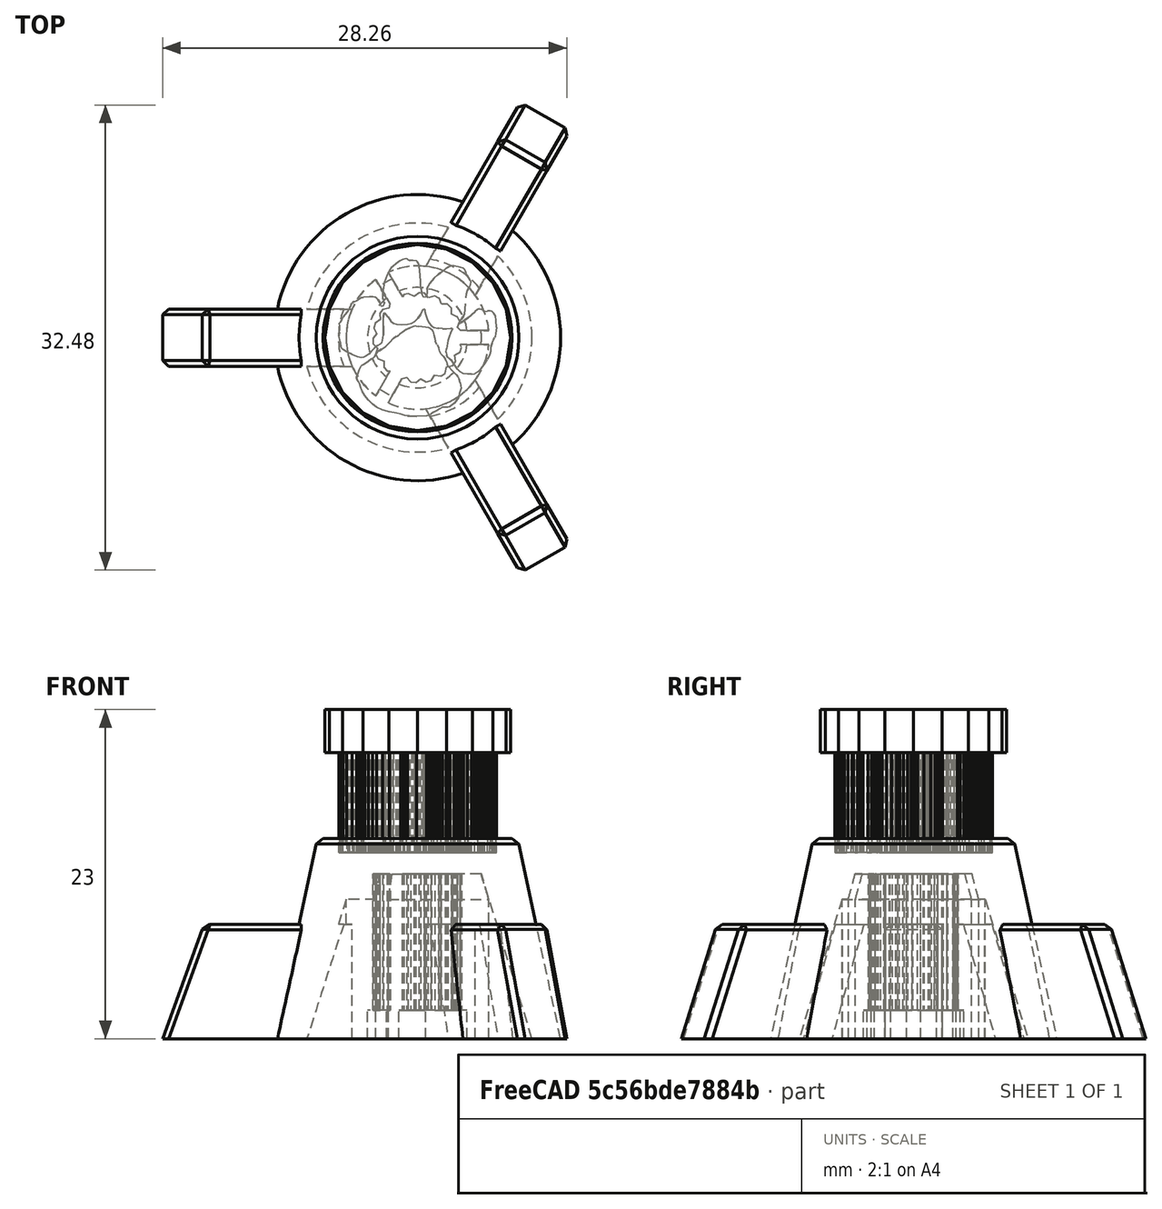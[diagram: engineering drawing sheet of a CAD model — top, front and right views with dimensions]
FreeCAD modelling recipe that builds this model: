
FCSTD DOCUMENT  (FreeCAD 0.18R16146 (Git))
Label: lcd-knob
License: All rights reserved
LicenseURL: http://en.wikipedia.org/wiki/All_rights_reserved
objects: Part::Feature×7, Part::Cut×4, Part::Cylinder×3, Part::MultiCommon×3, Part::Cone×2, Part::Box×2, Part::MultiFuse×2, Part::Chamfer×1
note: 24 computed .brp shape members not serialized (recipe doc carries the construction recipe); baked Part::Feature solids carry a one-line shape summary decoded from their .brp

FEATURE [Part::Feature] Powerful_Habbi001001_solid  label="hole"
  Placement = pos=(0.2,10.2,0) rot=(0,0,1;0rad)
  shape: bbox 7.502 x 7.501 x 12.43 mm, 81 faces (baked)
FEATURE [Part::Cylinder] Cylinder
  Angle = 360
  AttacherType = Attacher::AttachEngine3D
  Height = 17
  Radius = 3.5
FEATURE [Part::MultiCommon] Common  label="knob-hole"
  Shapes = -> [Cylinder,Powerful_Habbi001001_solid]
FEATURE [Part::Cone] Cone
  Angle = 360
  AttacherType = Attacher::AttachEngine3D
  Height = 14
  Radius1 = 10
  Radius2 = 7
FEATURE [Part::Cylinder] Cylinder001
  Angle = 360
  AttacherType = Attacher::AttachEngine3D
  Height = 13
  Radius = 5
FEATURE [Part::Cut] Cut
  Base = -> Cylinder001
  Tool = -> Common
FEATURE [Part::Cone] Cone001
  Angle = 360
  AttacherType = Attacher::AttachEngine3D
  Height = 13
  Radius1 = 8
  Radius2 = 4
FEATURE [Part::Cut] Cut001
  Base = -> Cone
  Tool = -> Cone001
FEATURE [Part::Box] Box  label="Cube"
  AttacherType = Attacher::AttachEngine3D
  Height = 12.43
  Length = 6
  Placement = pos=(0,-0.5,0) rot=(0,0,1;0rad)
  Width = 1
FEATURE [Part::Cut] Cut002
  Base = -> Cut
  Tool = -> Box
FEATURE [Part::Box] Box001  label="Cube001"
  AttacherType = Attacher::AttachEngine3D
  Height = 8
  Length = 14
  Placement = pos=(-18,-2,0) rot=(0,0,1;0rad)
  Width = 4
FEATURE [Part::Feature] Box002001  label="Cube003"
  Placement = pos=(0,0,2) rot=(0,0,1;0rad)
  shape: bbox 21.02 x 4 x 26.4 mm, 6 faces (baked)
FEATURE [Part::Cut] Cut003
  Base = -> Box001
  Tool = -> Box002001
FEATURE [Part::Feature] Cut003001  label="Cut004"
  Placement = pos=(0,0,0) rot=(0,0,1;4.18879rad)
  shape: bbox 10.38 x 13.98 x 8 mm, 6 faces (baked)
FEATURE [Part::Feature] Cut003002  label="Cut005"
  Placement = pos=(0,0,0) rot=(0,0,1;2.0944rad)
  shape: bbox 10.38 x 13.98 x 8 mm, 6 faces (baked)
FEATURE [Part::Feature] Cool_Trug_Allis001001_solid  label="paw"
  Placement = pos=(3.5,3.5,13) rot=(0,0,1;0rad)
  shape: bbox 13 x 13 x 10 mm, 407 faces (baked)
FEATURE [Part::Feature] Cut002001  label="Cut006"
  Placement = pos=(0,0,0) rot=(0,0,-1;2.0944rad)
  shape: bbox 10 x 10 x 13 mm, 63 faces (baked)
FEATURE [Part::Feature] Cut003003  label="Cut007"
  Placement = pos=(0,0,0) rot=(0,0,1;2.0944rad)
  shape: bbox 10 x 10 x 13 mm, 63 faces (baked)
FEATURE [Part::MultiCommon] Common001
  Shapes = -> [Cut003003,Cut002001]
FEATURE [Part::MultiCommon] Common002  label="core"
  Shapes = -> [Common001,Cut002]
FEATURE [Part::MultiFuse] Fusion
  Shapes = -> [Cut003002,Cut003001,Cut003,Cut001,Common002]
FEATURE [Part::Chamfer] Chamfer
  Base = -> Fusion
  Edges = 16 edges r=0.4: [Edge3,Edge4,Edge21,Edge22,Edge23,Edge24,Edge34,Edge35,Edge36,Edge37,Edge39,Edge44,Edge45,Edge46,Edge47,Edge49]
FEATURE [Part::Cylinder] Cylinder002
  Angle = 360
  AttacherType = Attacher::AttachEngine3D
  Height = 2.5
  Placement = pos=(0,0,11.5) rot=(0,0,1;0rad)
  Radius = 6
FEATURE [Part::MultiFuse] Fusion001
  Shapes = -> [Cylinder002,Chamfer]
